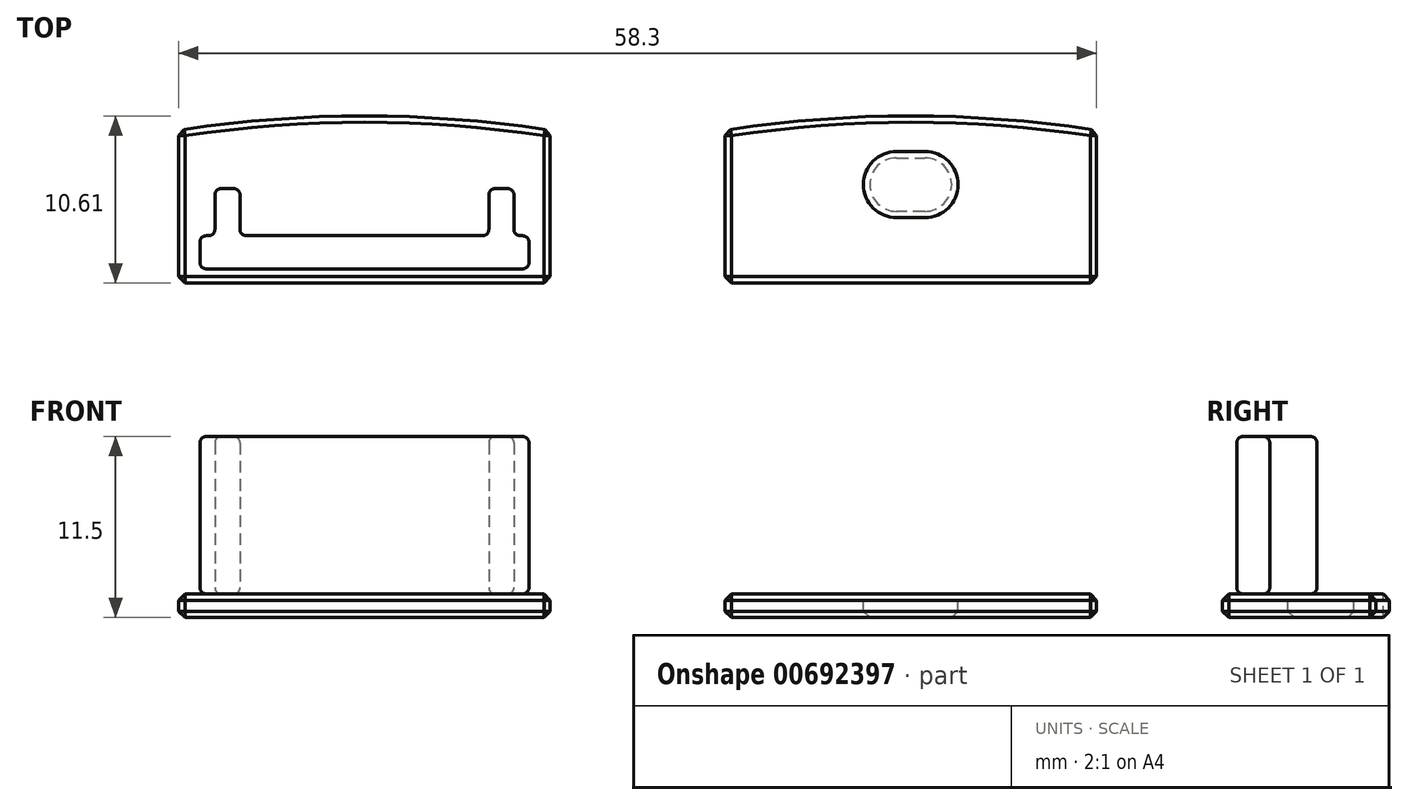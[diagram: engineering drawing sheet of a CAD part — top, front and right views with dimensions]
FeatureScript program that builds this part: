
annotation { "Feature Type Name" : "Feature", "Feature Type Description" : "" }
export const myFeature = defineFeature(function(context is Context, id is Id, definition is map)
    precondition{}
    {
        {
            var Q0;
            Q0=qCreatedBy(makeId("Top.planeOp"),FACE);
            var sketch = newSketch(context, id + "F0", { "sketchPlane" : qUnion([Q0])});
            skLineSegment(sketch, "E0.bottom", {"start": v(11.8, -4.85) * mm, "end": v(-11.8, -4.85) * mm});
            skLineSegment(sketch, "E0.top", {"start": v(11.8, 4.85) * mm, "end": v(-11.8, 4.85) * mm, "construction": true});
            skLineSegment(sketch, "E0.left", {"start": v(11.8, -4.85) * mm, "end": v(11.8, 4.85) * mm});
            skLineSegment(sketch, "E0.right", {"start": v(-11.8, -4.85) * mm, "end": v(-11.8, 4.85) * mm});
            skPoint(sketch, "E0.middle", {"position": v(0, 0) * mm});
            skLineSegment(sketch, "E1", {"start": v(-11.8, 5.76) * mm, "end": v(11.8, 5.76) * mm, "construction": true});
            skArc(sketch, "E2", {"start": v(-11.8, 4.85) * mm, "mid": v(0, -148.16) * mm, "end": v(11.8, 4.85) * mm, "construction": true});
            skArc(sketch, "E3", {"start": v(11.8, 4.85) * mm, "mid": v(0, 5.76) * mm, "end": v(-11.8, 4.85) * mm});
            skSolve(sketch);
        }
        {
            var Q0;
            Q0=makeQuery(id+"F0.imprint","IMPRINT",FACE,{"disambiguationData":[TD([[makeQuery(id+"F0.imprint","IMPRINT",EDGE,{"derivedFrom":sQuery(id+"F0.wireOp",EDGE,"E0.bottom")}),-1.0]])]});
            extrude(context, id + "F1", {"entities" : qUnion([Q0]), "depth" : 1.5 * mm, "offsetDistance" : 25 * mm});
        }
        {
            var Q0;
            Q0=makeQuery(id+"F1.opExtrude","CAP_FACE",FACE,{"disambiguationData":[OSD([sQuery(id+"F0.wireOp",EDGE,"E0.bottom"),sQuery(id+"F0.wireOp",EDGE,"E0.left"),sQuery(id+"F0.wireOp",EDGE,"E0.right"),sQuery(id+"F0.wireOp",EDGE,"E3")])],"isStart":false});
            var sketch = newSketch(context, id + "F2", { "sketchPlane" : qUnion([Q0])});
            skPoint(sketch, "E4.0", {"position": v(-11.8, -4.85) * mm});
            skLineSegment(sketch, "E5.bottom", {"start": v(-10.45, -3.95) * mm, "end": v(10.45, -3.95) * mm});
            skLineSegment(sketch, "E5.top", {"start": v(-10.45, -1.85) * mm, "end": v(-9.5, -1.85) * mm});
            skLineSegment(sketch, "E5.left", {"start": v(-10.45, -3.95) * mm, "end": v(-10.45, -1.85) * mm});
            skLineSegment(sketch, "E5.right", {"start": v(10.45, -3.95) * mm, "end": v(10.45, -1.85) * mm});
            skPoint(sketch, "E5.middle", {"position": v(0, -2.9) * mm});
            skLineSegment(sketch, "E6", {"start": v(0, 0) * mm, "end": v(0, 1.6) * mm, "construction": true});
            skLineSegment(sketch, "E7.bottom", {"start": v(-9.5, -1.85) * mm, "end": v(-7.9, -1.85) * mm, "construction": true});
            skLineSegment(sketch, "E7.top", {"start": v(-9.5, 1.15) * mm, "end": v(-7.9, 1.15) * mm});
            skLineSegment(sketch, "E7.left", {"start": v(-9.5, -1.85) * mm, "end": v(-9.5, 1.15) * mm});
            skLineSegment(sketch, "E7.right", {"start": v(-7.9, -1.85) * mm, "end": v(-7.9, 1.15) * mm});
            skPoint(sketch, "E7.middle", {"position": v(-8.7, -0.35) * mm});
            skLineSegment(sketch, "E8.MirrorCS", {"start": v(7.9, -1.85) * mm, "end": v(7.9, 1.15) * mm});
            skLineSegment(sketch, "E9.MirrorCS", {"start": v(9.5, 1.15) * mm, "end": v(7.9, 1.15) * mm});
            skLineSegment(sketch, "E10.MirrorCS", {"start": v(9.5, -1.85) * mm, "end": v(9.5, 1.15) * mm});
            skLineSegment(sketch, "E11.MirrorCS", {"start": v(9.5, -1.85) * mm, "end": v(7.9, -1.85) * mm, "construction": true});
            skLineSegment(sketch, "E12", {"start": v(-7.9, -1.85) * mm, "end": v(7.9, -1.85) * mm});
            skLineSegment(sketch, "E13", {"start": v(7.9, -1.85) * mm, "end": v(9.5, -1.85) * mm, "construction": true});
            skLineSegment(sketch, "E14", {"start": v(9.5, -1.85) * mm, "end": v(10.45, -1.85) * mm});
            skSolve(sketch);
        }
        {
            var Q0;
            Q0=makeQuery(id+"F2.imprint","IMPRINT",FACE,{"disambiguationData":[TD([[makeQuery(id+"F2.imprint","IMPRINT",EDGE,{"derivedFrom":sQuery(id+"F2.wireOp",EDGE,"E5.bottom")}),1.0]])]});
            extrude(context, id + "F3", {"entities" : qUnion([Q0]), "depth" : 10 * mm, "offsetDistance" : 25 * mm});
        }
        {
            var Q0;
            Q0=makeQuery(id+"F3.opExtrude","SWEPT_EDGE",EDGE,{"disambiguationData":[OSD([sQuery(id+"F2.wireOp",EDGE,"E7.top"),sQuery(id+"F2.wireOp",EDGE,"E7.right")])]});
            var Q1;
            Q1=makeQuery(id+"F3.opExtrude","SWEPT_EDGE",EDGE,{"disambiguationData":[OSD([sQuery(id+"F2.wireOp",EDGE,"E7.right"),sQuery(id+"F2.wireOp",EDGE,"E12")])]});
            var Q2;
            Q2=makeQuery(id+"F3.opExtrude","CAP_EDGE",EDGE,{"disambiguationData":[OSD([sQuery(id+"F2.wireOp",EDGE,"E12")])],"isStart":true});
            var Q3;
            Q3=makeQuery(id+"F3.opExtrude","CAP_EDGE",EDGE,{"disambiguationData":[OSD([sQuery(id+"F2.wireOp",EDGE,"E7.right")])],"isStart":true});
            var Q4;
            Q4=makeQuery(id+"F3.opExtrude","SWEPT_EDGE",EDGE,{"disambiguationData":[OSD([sQuery(id+"F2.wireOp",EDGE,"E8.MirrorCS"),sQuery(id+"F2.wireOp",EDGE,"E12")])]});
            var Q5;
            Q5=makeQuery(id+"F3.opExtrude","CAP_EDGE",EDGE,{"disambiguationData":[OSD([sQuery(id+"F2.wireOp",EDGE,"E8.MirrorCS")])],"isStart":true});
            var Q6;
            Q6=makeQuery(id+"F3.opExtrude","SWEPT_EDGE",EDGE,{"disambiguationData":[OSD([sQuery(id+"F2.wireOp",EDGE,"E8.MirrorCS"),sQuery(id+"F2.wireOp",EDGE,"E9.MirrorCS")])]});
            var Q7;
            Q7=makeQuery(id+"F3.opExtrude","SWEPT_EDGE",EDGE,{"disambiguationData":[OSD([sQuery(id+"F2.wireOp",EDGE,"E5.top"),sQuery(id+"F2.wireOp",EDGE,"E5.left")])]});
            var Q8;
            Q8=makeQuery(id+"F3.opExtrude","SWEPT_EDGE",EDGE,{"disambiguationData":[OSD([sQuery(id+"F2.wireOp",EDGE,"E5.bottom"),sQuery(id+"F2.wireOp",EDGE,"E5.left")])]});
            var Q9;
            Q9=makeQuery(id+"F3.opExtrude","SWEPT_EDGE",EDGE,{"disambiguationData":[OSD([sQuery(id+"F2.wireOp",EDGE,"E5.bottom"),sQuery(id+"F2.wireOp",EDGE,"E5.right")])]});
            var Q10;
            Q10=makeQuery(id+"F3.opExtrude","SWEPT_EDGE",EDGE,{"disambiguationData":[OSD([sQuery(id+"F2.wireOp",EDGE,"E5.right"),sQuery(id+"F2.wireOp",EDGE,"E14")])]});
            var Q11;
            Q11=makeQuery(id+"F3.opExtrude","CAP_FACE",FACE,{"disambiguationData":[OSD([sQuery(id+"F2.wireOp",EDGE,"E5.bottom"),sQuery(id+"F2.wireOp",EDGE,"E5.top"),sQuery(id+"F2.wireOp",EDGE,"E5.left"),sQuery(id+"F2.wireOp",EDGE,"E5.right"),sQuery(id+"F2.wireOp",EDGE,"E7.top"),sQuery(id+"F2.wireOp",EDGE,"E7.left"),sQuery(id+"F2.wireOp",EDGE,"E7.right"),sQuery(id+"F2.wireOp",EDGE,"E8.MirrorCS"),sQuery(id+"F2.wireOp",EDGE,"E9.MirrorCS"),sQuery(id+"F2.wireOp",EDGE,"E10.MirrorCS"),sQuery(id+"F2.wireOp",EDGE,"E12"),sQuery(id+"F2.wireOp",EDGE,"E14")])],"isStart":false});
            var Q12;
            Q12=makeQuery(id+"F3.opExtrude","CAP_FACE",FACE,{"disambiguationData":[OSD([sQuery(id+"F2.wireOp",EDGE,"E5.bottom"),sQuery(id+"F2.wireOp",EDGE,"E5.top"),sQuery(id+"F2.wireOp",EDGE,"E5.left"),sQuery(id+"F2.wireOp",EDGE,"E5.right"),sQuery(id+"F2.wireOp",EDGE,"E7.top"),sQuery(id+"F2.wireOp",EDGE,"E7.left"),sQuery(id+"F2.wireOp",EDGE,"E7.right"),sQuery(id+"F2.wireOp",EDGE,"E8.MirrorCS"),sQuery(id+"F2.wireOp",EDGE,"E9.MirrorCS"),sQuery(id+"F2.wireOp",EDGE,"E10.MirrorCS"),sQuery(id+"F2.wireOp",EDGE,"E12"),sQuery(id+"F2.wireOp",EDGE,"E14")])],"isStart":true});
            var Q13;
            Q13=makeQuery(id+"F3.opExtrude","SWEPT_FACE",FACE,{"disambiguationData":[OSD([sQuery(id+"F2.wireOp",EDGE,"E10.MirrorCS")])]});
            var Q14;
            Q14=makeQuery(id+"F3.opExtrude","SWEPT_FACE",FACE,{"disambiguationData":[OSD([sQuery(id+"F2.wireOp",EDGE,"E7.left")])]});
            fillet(context, id + "F4", {"entities" : qUnion([Q0, Q1, Q2, Q3, Q4, Q5, Q6, Q7, Q8, Q9, Q10, Q11, Q12, Q13, Q14]), "radius" : 0.4 * mm, "tangentPropagation" : true, "allowEdgeOverflow" : false});
        }
        {
            var Q0;
            Q0=makeQuery(id+"F1.opExtrude","CAP_FACE",FACE,{"disambiguationData":[OSD([sQuery(id+"F0.wireOp",EDGE,"E0.bottom"),sQuery(id+"F0.wireOp",EDGE,"E0.left"),sQuery(id+"F0.wireOp",EDGE,"E0.right"),sQuery(id+"F0.wireOp",EDGE,"E3")])],"isStart":true});
            var Q1;
            Q1=makeQuery(id+"F1.opExtrude","SWEPT_EDGE",EDGE,{"disambiguationData":[OSD([sQuery(id+"F0.wireOp",EDGE,"E0.bottom"),sQuery(id+"F0.wireOp",EDGE,"E0.right")])]});
            var Q2;
            Q2=makeQuery(id+"F1.opExtrude","SWEPT_EDGE",EDGE,{"disambiguationData":[OSD([sQuery(id+"F0.wireOp",EDGE,"E0.bottom"),sQuery(id+"F0.wireOp",EDGE,"E0.left")])]});
            var Q3;
            Q3=makeQuery(id+"F1.opExtrude","SWEPT_EDGE",EDGE,{"disambiguationData":[OSD([sQuery(id+"F0.wireOp",EDGE,"E0.left"),sQuery(id+"F0.wireOp",EDGE,"E3")])]});
            var Q4;
            Q4=makeQuery(id+"F1.opExtrude","SWEPT_EDGE",EDGE,{"disambiguationData":[OSD([sQuery(id+"F0.wireOp",EDGE,"E0.right"),sQuery(id+"F0.wireOp",EDGE,"E3")])]});
            var Q5;
            Q5=makeQuery(id+"F1.opExtrude","CAP_EDGE",EDGE,{"disambiguationData":[OSD([sQuery(id+"F0.wireOp",EDGE,"E3")])],"isStart":false});
            var Q6;
            Q6=makeQuery(id+"F1.opExtrude","CAP_EDGE",EDGE,{"disambiguationData":[OSD([sQuery(id+"F0.wireOp",EDGE,"E0.right")])],"isStart":false});
            var Q7;
            Q7=makeQuery(id+"F1.opExtrude","CAP_EDGE",EDGE,{"disambiguationData":[OSD([sQuery(id+"F0.wireOp",EDGE,"E0.bottom")])],"isStart":false});
            var Q8;
            Q8=makeQuery(id+"F1.opExtrude","CAP_EDGE",EDGE,{"disambiguationData":[OSD([sQuery(id+"F0.wireOp",EDGE,"E0.left")])],"isStart":false});
            chamfer(context, id + "F5", {"entities" : qUnion([Q0, Q1, Q2, Q3, Q4, Q5, Q6, Q7, Q8]), "width" : 0.4 * mm, "tangentPropagation" : true});
        }
        {
            var Q0;
            Q0=makeQuery(id+"F1.opExtrude","SWEPT_BODY",BODY,{"disambiguationData":[OSD([sQuery(id+"F0.wireOp",EDGE,"E0.bottom"),sQuery(id+"F0.wireOp",EDGE,"E0.left"),sQuery(id+"F0.wireOp",EDGE,"E0.right"),sQuery(id+"F0.wireOp",EDGE,"E3")])]});
            transform(context, id + "F6", {"entities" : qUnion([Q0]), "transformType" : TransformType.TRANSLATION_3D, "dx" : 34.7 * mm, "dy" : 0 * mm, "dz" : 0 * mm, "makeCopy" : true});
        }
        {
            var Q0;
            Q0=makeQuery(id+"F6.opPattern","COPY",FACE,{"derivedFrom":makeQuery(id+"F1.opExtrude","CAP_FACE",FACE,{"disambiguationData":[OSD([sQuery(id+"F0.wireOp",EDGE,"E0.bottom"),sQuery(id+"F0.wireOp",EDGE,"E0.left"),sQuery(id+"F0.wireOp",EDGE,"E0.right"),sQuery(id+"F0.wireOp",EDGE,"E3")])],"isStart":false}),"instanceName":"1"});
            var sketch = newSketch(context, id + "F7", { "sketchPlane" : qUnion([Q0])});
            skPoint(sketch, "E15", {"position": v(34.7, 1.4) * mm});
            skPoint(sketch, "E15.positionSnap0", {"position": v(34.7, -4.45) * mm});
            skPoint(sketch, "E15.positionSnap1", {"position": v(23.3, 0.03) * mm});
            skLineSegment(sketch, "E16", {"start": v(33.8, 1.4) * mm, "end": v(35.6, 1.4) * mm, "construction": true});
            skArc(sketch, "E17.0.startCap", {"start": v(33.8, -0.7) * mm, "mid": v(31.7, 1.4) * mm, "end": v(33.8, 3.5) * mm});
            skArc(sketch, "E17.0.endCap", {"start": v(35.6, 3.5) * mm, "mid": v(37.7, 1.4) * mm, "end": v(35.6, -0.7) * mm});
            skLineSegment(sketch, "E17.0.left", {"start": v(33.8, 3.5) * mm, "end": v(35.6, 3.5) * mm});
            skLineSegment(sketch, "E17.0.right", {"start": v(33.8, -0.7) * mm, "end": v(35.6, -0.7) * mm});
            skSolve(sketch);
        }
        {
            var Q0;
            Q0=makeQuery(id+"F7.imprint","IMPRINT",FACE,{"disambiguationData":[TD([[makeQuery(id+"F7.imprint","IMPRINT",EDGE,{"derivedFrom":sQuery(id+"F7.wireOp",EDGE,"E17.0.startCap")}),-1.0]])]});
            extrude(context, id + "F8", {"entities" : qUnion([Q0]), "operationType" : NewBodyOperationType.REMOVE, "endBound" : BoundingType.THROUGH_ALL, "oppositeDirection" : true, "depth" : 25 * mm, "offsetDistance" : 25 * mm});
        }
        {
            var Q0;
            Q0=makeQuery(id+"F8.boolean.opBoolean","COPY",EDGE,{"derivedFrom":makeQuery(id+"F8.opExtrude","CAP_EDGE",EDGE,{"disambiguationData":[OSD([sQuery(id+"F7.wireOp",EDGE,"E17.0.startCap")])],"isStart":true})});
            var Q1;
            Q1=makeQuery(id+"F8.boolean.opBoolean","INTERSECT",EDGE,{"derivedFrom":[makeQuery(id+"F6.opPattern","COPY",FACE,{"derivedFrom":makeQuery(id+"F1.opExtrude","CAP_FACE",FACE,{"disambiguationData":[OSD([sQuery(id+"F0.wireOp",EDGE,"E0.bottom"),sQuery(id+"F0.wireOp",EDGE,"E0.left"),sQuery(id+"F0.wireOp",EDGE,"E0.right"),sQuery(id+"F0.wireOp",EDGE,"E3")])],"isStart":true}),"instanceName":"1"}),makeQuery(id+"F8.opExtrude","SWEPT_FACE",FACE,{"disambiguationData":[OSD([sQuery(id+"F7.wireOp",EDGE,"E17.0.endCap")])]})]});
            chamfer(context, id + "F9", {"entities" : qUnion([Q0, Q1]), "width" : 0.4 * mm, "tangentPropagation" : true});
        }
    });
